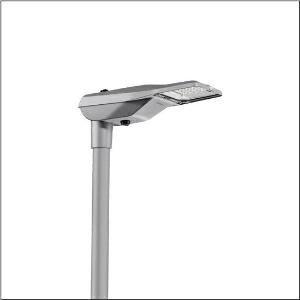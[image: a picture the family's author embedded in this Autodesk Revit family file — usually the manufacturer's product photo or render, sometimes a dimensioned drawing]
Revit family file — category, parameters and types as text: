
# Revit family: streetlight_sl_21_iq_micro___st1_5a_5xe1p31y08db_002f
name_source: partatom
category: Lighting Fixtures
units: mm (PartAtom-declared; Revit-internal decimal feet)

## family parameters
Cut with Voids When Loaded = No
Host = Face
Light Source = No
Part Type = Normal
Room Calculation Point = No
Round Connector Dimension = Use Diameter
Shared = No

## types (1)
- --- (1 x LED, 5030 lm, 39.1 W, 3000K)
    Apparent Load = 39 VA
    CIE Flux Codes = 22 53 95 100 100
    Color Rendering = 70
    Color Temperature = 3000K
    Default Elevation = 1800 mm
    Description = Streetlight SL 21 iQ micro, mast luminaire, primary light control with lens, of PMMA, primary optical cover: cover, of toughened safety glass, transparent, light distribution: ST1.5a, light emission: direct distribution, primary light characteristic: asymmetric, installation type: post-top, side-entry, LED, High Power LED, rated luminous flux: 5.030lm, luminous efficacy: 129lm/W, light colour: 730, colour temperature: 3000K, control: presetting dimming logarithmic, Street-Remote, Auto-Match, Temp-Guard, Lumen-Switch, Night-Set, Smart-Wire, Light-Fading, Desk-Remote (wireless, voltage-free reading and setting of iQ features in the workshop via application-optimized NFC function/RFID function), optimised constant luminous flux control (CLO 2.0), mains connection: 220..240V, AC, 50/60Hz, start of lifetime: 39W, end of service life: 41W, reduction: 17W, luminaire housing, of diecast aluminium, powder-coated, Siteco® metallic grey (DB 702S), corrosivity category C5 mid according to DIN EN ISO 12944, please order mast flange separately, inclination adjustable: 0°, 5°, 10°, 15°, sealing non-destructively replaceable, multi-level sealing system, length: 528mm, width: 235mm, height: 110mm, mast flange for spigot size: 42mm (side-entry): 5XC10008XM4, 60/48mm (side-entry/post-top): 5XC10108XM2, 76/60mm (side-entry/post-top): 5XC10108XM1, Smart Interface below and above, protection rating (complete): IP66, insulation class (complete): insulation class II (safety insulation), certification: CE, ENEC, ENEC+, VDE, impact resistance: IK09, permissible operating ambient temperature for outdoor applications: -40..+50°C, standard-compliant lighting for roads and squares, packaging unit: 1 piece

Light Distribution: ST1.5a
    Height = 110 mm
    Lamp = 1 x LED
    Lamp Light Flux = 5030 lm
    Lamp Power = 39.1 W
    Lamp count = 1
    Length = 528 mm
    Luminous efficacy = 129 lm/W
    Manufacturer = Siteco
    ModVariant = No
    Model = 5XE1P31Y08DB
    Number of Poles = 1
    OnlyDefault = Yes
    Power Factor = 1
    Product Name = Streetlight SL 21 iQ micro | ST1.5a
    Product group = mast luminaire | pylon top
    ProductGroupID = 6100
    Protection Class = Protection class II
    Protection Degree = IP 66
    RLX_Detail_Level = 1
    RLX_Emergency_Light_Flux = 0 lm
    RLX_Emergency_Type = 0
    RLX_Emergency_Type_DB = No
    RlxData = <blob elided: 103373 chars, md5=c3676689>
    Socket = socket
    Standby Power = 0 W
    System Light Flux = 5030 lm
    System Power = 39 W
    Type Comments = factory setting: luminous flux: 100 % | dim-lin: 254 | 765 mA
    Type Image = l_1007239.jpg
    URL = http://relux.com
    VarID = @adj_042065
    Voltage = 0 V
    Weight = 0.00 kg
    Width = 235 mm

## geometry (parser evidence)
native form markers: Blend x4, Sweep x12
no freeform markers — native parametric forms only
